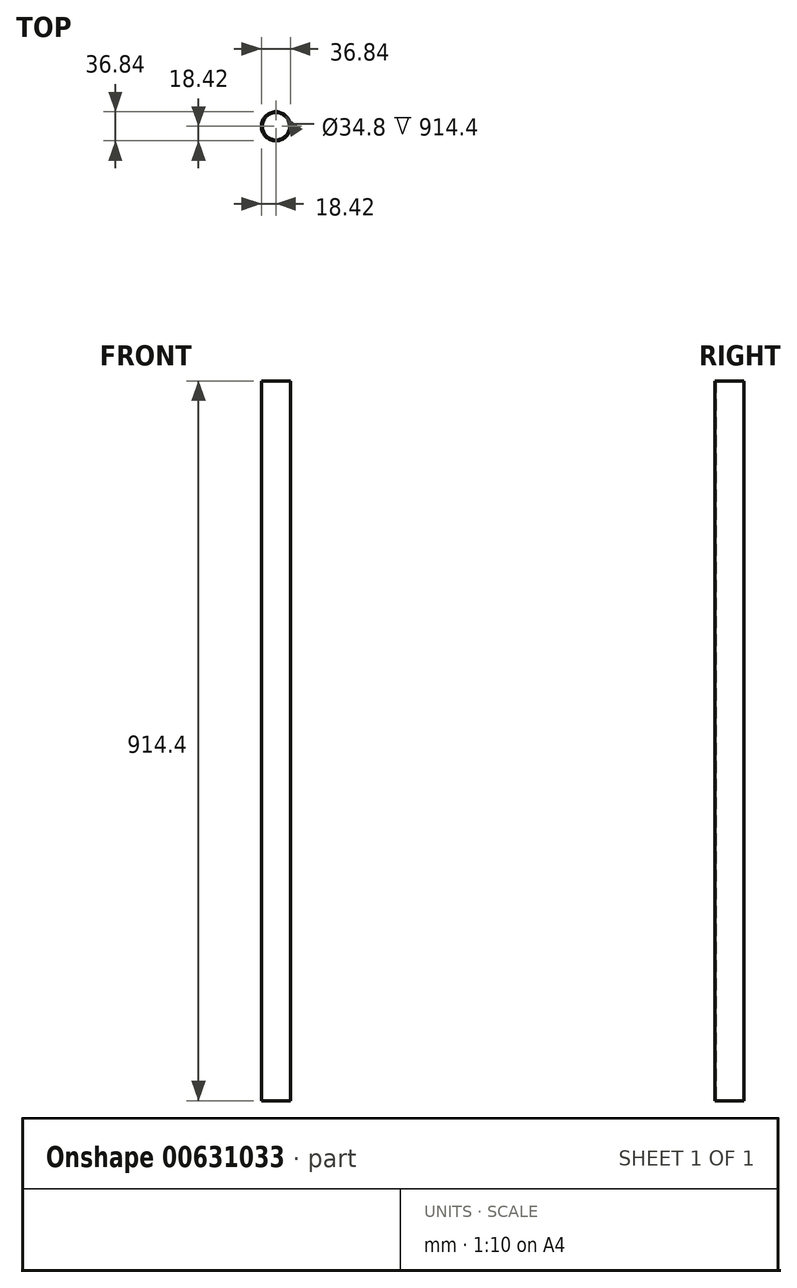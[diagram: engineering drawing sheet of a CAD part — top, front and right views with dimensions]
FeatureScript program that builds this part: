
annotation { "Feature Type Name" : "Feature", "Feature Type Description" : "" }
export const myFeature = defineFeature(function(context is Context, id is Id, definition is map)
    precondition{}
    {
        {
            var Q0;
            Q0=qCreatedBy(makeId("Top.planeOp"),FACE);
            var sketch = newSketch(context, id + "F0", { "sketchPlane" : qUnion([Q0])});
            skCircle(sketch, "E0", {"center": v(0, 0) * mm, "radius": 18.41 * mm});
            skCircle(sketch, "E1", {"center": v(0, 0) * mm, "radius": 17.4 * mm});
            skSolve(sketch);
        }
        {
            var Q0;
            Q0=makeQuery(id+"F0.imprint","IMPRINT",FACE,{"disambiguationData":[TD([[makeQuery(id+"F0.imprint","IMPRINT",EDGE,{"derivedFrom":sQuery(id+"F0.wireOp",EDGE,"E0")}),1.0]])]});
            extrude(context, id + "F1", {"entities" : qUnion([Q0]), "depth" : 914.4 * mm, "offsetDistance" : 25.4 * mm});
        }
    });
